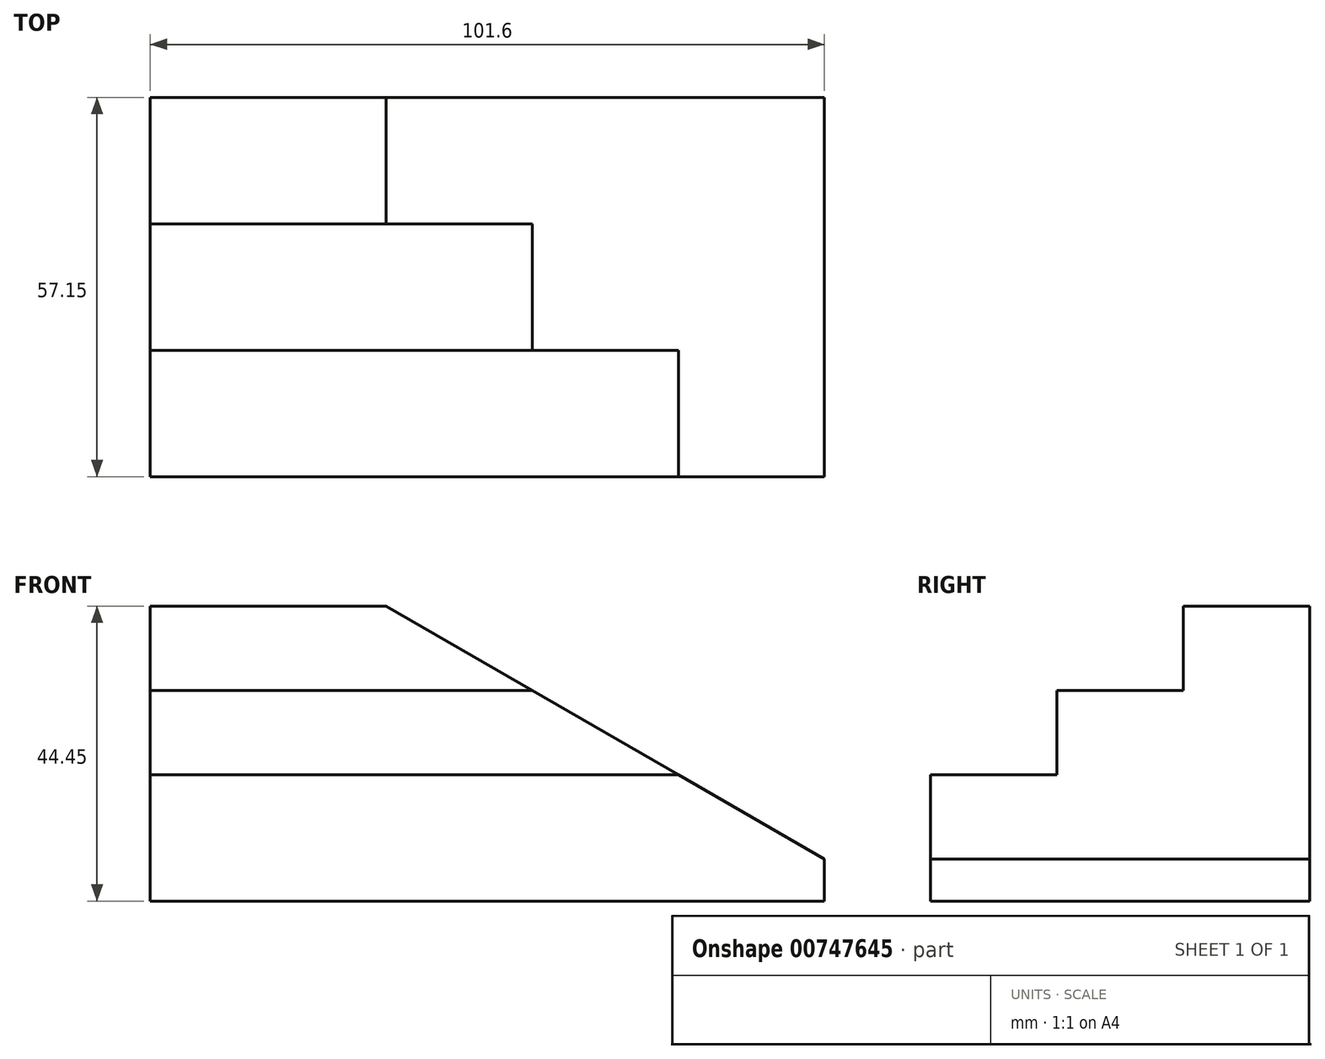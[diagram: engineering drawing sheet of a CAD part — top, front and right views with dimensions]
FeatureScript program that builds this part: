
annotation { "Feature Type Name" : "Feature", "Feature Type Description" : "" }
export const myFeature = defineFeature(function(context is Context, id is Id, definition is map)
    precondition{}
    {
        {
            var Q0;
            Q0=qCreatedBy(makeId("Right.planeOp"),FACE);
            var sketch = newSketch(context, id + "F0", { "sketchPlane" : qUnion([Q0])});
            skLineSegment(sketch, "E0", {"start": v(0, 44.45) * mm, "end": v(-19.05, 44.45) * mm});
            skLineSegment(sketch, "E1", {"start": v(-38.1, 31.75) * mm, "end": v(-19.05, 31.75) * mm});
            skLineSegment(sketch, "E2", {"start": v(-57.15, 19.05) * mm, "end": v(-38.1, 19.05) * mm});
            skLineSegment(sketch, "E3", {"start": v(-19.05, 44.45) * mm, "end": v(-19.05, 31.75) * mm});
            skLineSegment(sketch, "E4", {"start": v(-38.1, 31.75) * mm, "end": v(-38.1, 19.05) * mm});
            skLineSegment(sketch, "E5", {"start": v(0, 0) * mm, "end": v(0, 6.35) * mm});
            skLineSegment(sketch, "E6", {"start": v(0, 6.35) * mm, "end": v(-57.15, 6.35) * mm});
            skLineSegment(sketch, "E7", {"start": v(-57.15, 6.35) * mm, "end": v(-57.15, 0) * mm});
            skLineSegment(sketch, "E8", {"start": v(-57.15, 0) * mm, "end": v(0, 0) * mm});
            skLineSegment(sketch, "E9", {"start": v(-57.15, 19.05) * mm, "end": v(-57.15, 6.35) * mm});
            skLineSegment(sketch, "E10", {"start": v(0, 44.45) * mm, "end": v(0, 6.35) * mm});
            skSolve(sketch);
        }
        {
            var Q0;
            Q0=makeQuery(id+"F0.imprint","IMPRINT",FACE,{"disambiguationData":[TD([[makeQuery(id+"F0.imprint","IMPRINT",EDGE,{"derivedFrom":sQuery(id+"F0.wireOp",EDGE,"E0")}),1.0]])]});
            var Q1;
            Q1=makeQuery(id+"F0.imprint","IMPRINT",FACE,{"disambiguationData":[TD([[makeQuery(id+"F0.imprint","IMPRINT",EDGE,{"derivedFrom":sQuery(id+"F0.wireOp",EDGE,"E5")}),1.0]])]});
            extrude(context, id + "F1", {"entities" : qUnion([Q0, Q1]), "depth" : 101.6 * mm, "offsetDistance" : 25.4 * mm});
        }
        {
            var Q0;
            Q0=qCreatedBy(makeId("Front.planeOp"),FACE);
            var sketch = newSketch(context, id + "F2", { "sketchPlane" : qUnion([Q0])});
            skLineSegment(sketch, "E11", {"start": v(35.56, 44.45) * mm, "end": v(101.6, 44.45) * mm});
            skLineSegment(sketch, "E12", {"start": v(101.6, 44.45) * mm, "end": v(101.6, 6.35) * mm});
            skLineSegment(sketch, "E13", {"start": v(35.56, 44.45) * mm, "end": v(101.6, 6.35) * mm});
            skSolve(sketch);
        }
        {
            var Q0;
            Q0 = qSketchRegion(id + "F2", true);
            extrude(context, id + "F3", {"entities" : qUnion([Q0]), "operationType" : NewBodyOperationType.REMOVE, "depth" : 57.15 * mm, "offsetDistance" : 25.4 * mm});
        }
    });
